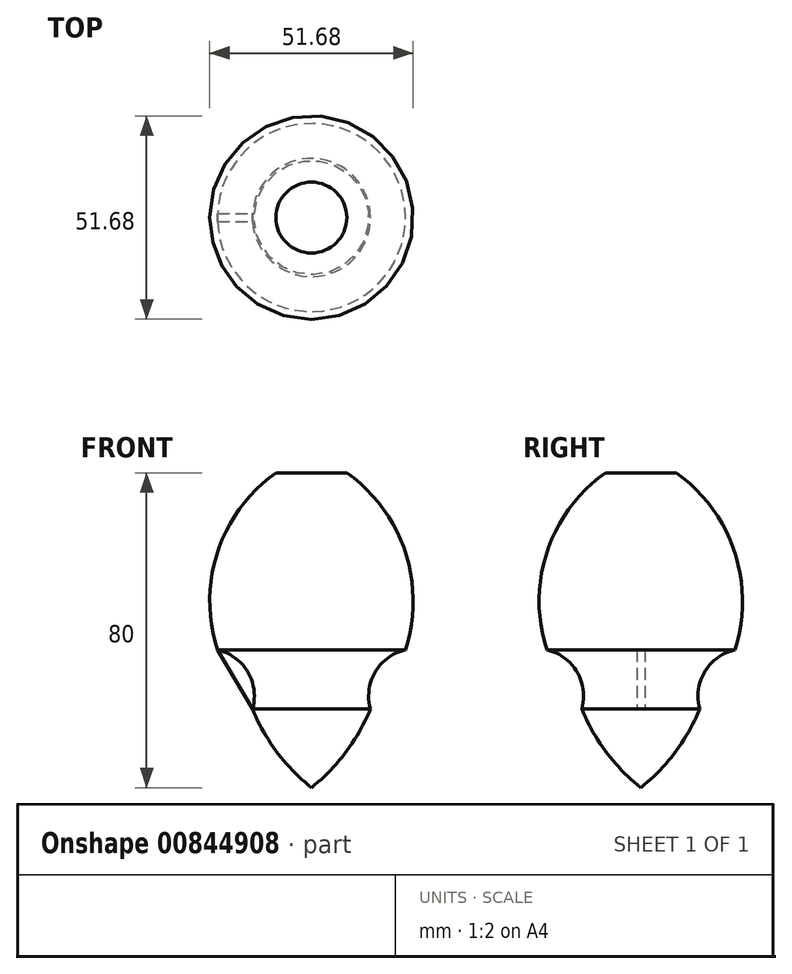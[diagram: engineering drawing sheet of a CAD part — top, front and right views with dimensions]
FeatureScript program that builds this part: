
annotation { "Feature Type Name" : "Feature", "Feature Type Description" : "" }
export const myFeature = defineFeature(function(context is Context, id is Id, definition is map)
    precondition{}
    {
        {
            var Q0;
            Q0=qCreatedBy(makeId("Front.planeOp"),FACE);
            var sketch = newSketch(context, id + "F0", { "sketchPlane" : qUnion([Q0])});
            skLineSegment(sketch, "E0", {"start": v(0, 0) * mm, "end": v(0, 80) * mm});
            skLineSegment(sketch, "E1", {"start": v(0, 80) * mm, "end": v(9, 80) * mm});
            skLineSegment(sketch, "E2", {"start": v(0, 20) * mm, "end": v(15, 20) * mm});
            skLineSegment(sketch, "E3", {"start": v(0, 35) * mm, "end": v(23.88, 35) * mm});
            skArc(sketch, "E4", {"start": v(23.88, 35) * mm, "mid": v(23.82, 59.94) * mm, "end": v(9, 80) * mm});
            skArc(sketch, "E5", {"start": v(23.88, 35) * mm, "mid": v(16.21, 29.41) * mm, "end": v(15, 20) * mm});
            skArc(sketch, "E6", {"start": v(0, 0) * mm, "mid": v(8.77, 9.05) * mm, "end": v(15, 20) * mm});
            skSolve(sketch);
        }
        {
            var Q0;
            {var subQ0=sQuery(id+"F0.wireOp",EDGE,"E1");Q0=makeQuery(id+"F0.imprint","IMPRINT",FACE,{"disambiguationData":[TD([[makeQuery(id+"F0.imprint","IMPRINT",EDGE,{"derivedFrom":subQ0}),-1.0]])]});}
            var Q1;
            {var subQ0=sQuery(id+"F0.wireOp",EDGE,"E2");Q1=makeQuery(id+"F0.imprint","IMPRINT",FACE,{"disambiguationData":[TD([[makeQuery(id+"F0.imprint","IMPRINT",EDGE,{"derivedFrom":subQ0}),1.0]])]});}
            var Q2;
            {var subQ2=sQuery(id+"F0.wireOp",EDGE,"E2");Q2=makeQuery(id+"F0.imprint","IMPRINT",FACE,{"disambiguationData":[TD([[makeQuery(id+"F0.imprint","IMPRINT",EDGE,{"derivedFrom":subQ2}),-1.0]])]});}
            var Q3;
            Q3=sQuery(id+"F0.wireOp",EDGE,"E0");
            revolve(context, id + "F1", {"surfaceOperationType" : NewSurfaceOperationType.NEW, "entities" : qUnion([Q0, Q1, Q2]), "axis" : qUnion([Q3]), "revolveType" : RevolveType.FULL});
        }
        {
            var Q0;
            Q0=qCreatedBy(makeId("Front.planeOp"),FACE);
            var sketch = newSketch(context, id + "F2", { "sketchPlane" : qUnion([Q0])});
            skLineSegment(sketch, "E7.0", {"start": v(23.88, 35) * mm, "end": v(-23.88, 35) * mm});
            skLineSegment(sketch, "E8.0", {"start": v(15, 20) * mm, "end": v(-15, 20) * mm});
            skLineSegment(sketch, "E9", {"start": v(-23.88, 35) * mm, "end": v(-15, 20) * mm});
            skLineSegment(sketch, "E10", {"start": v(0, 20) * mm, "end": v(0, 35) * mm});
            skSolve(sketch);
        }
        {
            var Q0;
            {var subQ0=sQuery(id+"F2.wireOp",EDGE,"E9");Q0=makeQuery(id+"F2.imprint","IMPRINT",FACE,{"disambiguationData":[TD([[makeQuery(id+"F2.imprint","IMPRINT",EDGE,{"derivedFrom":subQ0}),1.0]])]});}
            extrude(context, id + "F3", {"entities" : qUnion([Q0]), "operationType" : NewBodyOperationType.ADD, "endBound" : BoundingType.SYMMETRIC, "depth" : 2 * mm, "offsetDistance" : 25 * mm});
        }
    });
